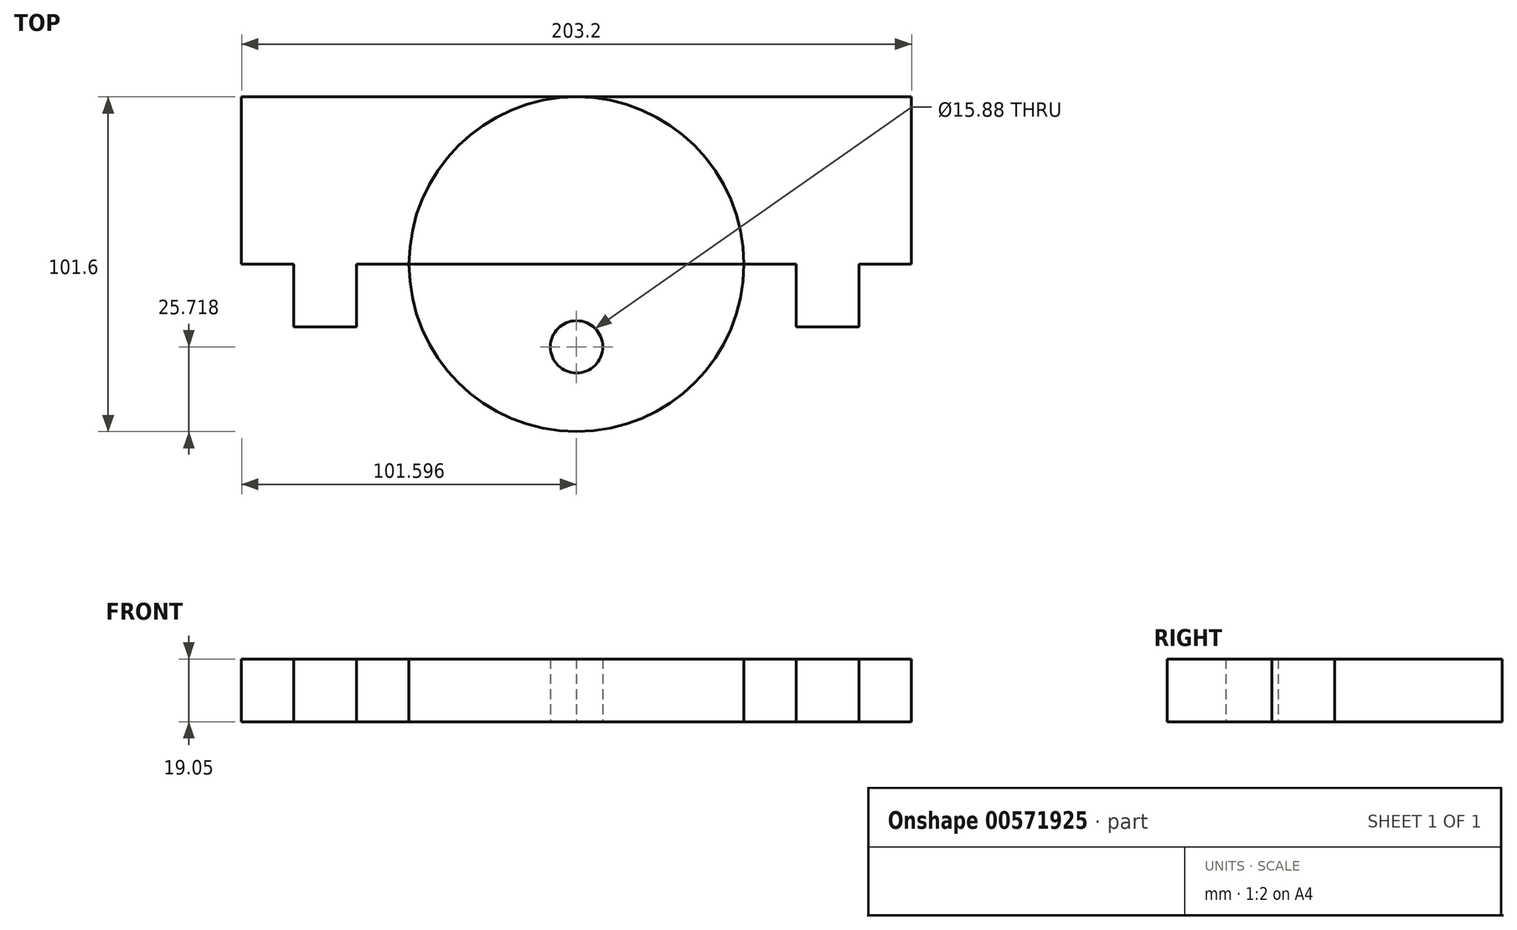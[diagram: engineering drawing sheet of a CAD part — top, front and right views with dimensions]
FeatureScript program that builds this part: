
annotation { "Feature Type Name" : "Feature", "Feature Type Description" : "" }
export const myFeature = defineFeature(function(context is Context, id is Id, definition is map)
    precondition{}
    {
        {
            var Q0;
            Q0=qCreatedBy(makeId("Top.planeOp"),FACE);
            var sketch = newSketch(context, id + "F0", { "sketchPlane" : qUnion([Q0])});
            skLineSegment(sketch, "E0.bottom", {"start": v(-100.72, 0) * mm, "end": v(-303.92, 0) * mm});
            skLineSegment(sketch, "E0.top", {"start": v(-100.72, -50.8) * mm, "end": v(-303.92, -50.8) * mm});
            skLineSegment(sketch, "E0.left", {"start": v(-100.72, 0) * mm, "end": v(-100.72, -50.8) * mm});
            skLineSegment(sketch, "E0.right", {"start": v(-303.92, 0) * mm, "end": v(-303.92, -50.8) * mm});
            skCircle(sketch, "E1", {"center": v(-202.32, -50.8) * mm, "radius": 50.8 * mm});
            skCircle(sketch, "E2", {"center": v(-202.32, -75.88) * mm, "radius": 7.94 * mm});
            skSolve(sketch);
        }
        {
            var Q0;
            {var subQ0=sQuery(id+"F0.wireOp",EDGE,"E0.right");Q0=makeQuery(id+"F0.imprint","IMPRINT",FACE,{"disambiguationData":[TD([[makeQuery(id+"F0.imprint","IMPRINT",EDGE,{"derivedFrom":subQ0}),1.0]])]});}
            var Q1;
            {var subQ0=sQuery(id+"F0.wireOp",EDGE,"E1");var subQ1=sQuery(id+"F0.wireOp",EDGE,"E0.top");var subQ2=makeQuery(id+"F0.imprint","INTERSECT",VERTEX,{"disambiguationData":[OD(0.0)],"derivedFrom":[subQ1,subQ0]});Q1=makeQuery(id+"F0.imprint","IMPRINT",FACE,{"disambiguationData":[TD([[makeQuery(id+"F0.imprint","IMPRINT",EDGE,{"disambiguationData":[TD([[subQ2,-1.0]])],"derivedFrom":subQ1}),-1.0]])]});}
            var Q2;
            {var subQ0=sQuery(id+"F0.wireOp",EDGE,"E0.left");Q2=makeQuery(id+"F0.imprint","IMPRINT",FACE,{"disambiguationData":[TD([[makeQuery(id+"F0.imprint","IMPRINT",EDGE,{"derivedFrom":subQ0}),-1.0]])]});}
            var Q3;
            Q3=makeQuery(id+"F0.imprint","IMPRINT",FACE,{"disambiguationData":[TD([[makeQuery(id+"F0.imprint","IMPRINT",EDGE,{"derivedFrom":sQuery(id+"F0.wireOp",EDGE,"E2")}),-1.0]])]});
            extrude(context, id + "F1", {"entities" : qUnion([Q0, Q1, Q2, Q3]), "depth" : 19.05 * mm, "offsetDistance" : 25.4 * mm});
        }
        {
            var Q0;
            {var subQ0=sQuery(id+"F0.wireOp",EDGE,"E0.top");Q0=makeQuery(id+"F1.opExtrude","SWEPT_FACE",FACE,{"disambiguationData":[OSD([subQ0]),TDD([makeQuery(id+"F0.imprint","IMPRINT",EDGE,{"disambiguationData":[TD([[makeQuery(id+"F0.imprint","INTERSECT",VERTEX,{"derivedFrom":[subQ0,sQuery(id+"F0.wireOp",EDGE,"E0.right")]}),1.0]])],"derivedFrom":subQ0})])]});}
            var sketch = newSketch(context, id + "F2", { "sketchPlane" : qUnion([Q0])});
            skLineSegment(sketch, "E3.bottom", {"start": v(-288.05, 19.05) * mm, "end": v(-269, 19.05) * mm});
            skLineSegment(sketch, "E3.top", {"start": v(-288.05, 0) * mm, "end": v(-269, 0) * mm});
            skLineSegment(sketch, "E3.left", {"start": v(-288.05, 19.05) * mm, "end": v(-288.05, 0) * mm});
            skLineSegment(sketch, "E3.right", {"start": v(-269, 19.05) * mm, "end": v(-269, 0) * mm});
            skLineSegment(sketch, "E4.bottom", {"start": v(-135.65, 19.05) * mm, "end": v(-116.6, 19.05) * mm});
            skLineSegment(sketch, "E4.top", {"start": v(-135.65, 0) * mm, "end": v(-116.6, 0) * mm});
            skLineSegment(sketch, "E4.left", {"start": v(-135.65, 19.05) * mm, "end": v(-135.65, 0) * mm});
            skLineSegment(sketch, "E4.right", {"start": v(-116.6, 19.05) * mm, "end": v(-116.6, 0) * mm});
            skLineSegment(sketch, "E5.0.0", {"start": v(-303.92, 19.05) * mm, "end": v(-253.12, 19.05) * mm});
            skLineSegment(sketch, "E5.0.1", {"start": v(-253.12, 19.05) * mm, "end": v(-151.52, 19.05) * mm});
            skLineSegment(sketch, "E5.0.2", {"start": v(-151.52, 19.05) * mm, "end": v(-100.72, 19.05) * mm});
            skLineSegment(sketch, "E5.0.4", {"start": v(-100.72, 19.05) * mm, "end": v(-303.92, 19.05) * mm});
            skSolve(sketch);
        }
        {
            var Q0;
            Q0=makeQuery(id+"F2.imprint","IMPRINT",FACE,{"disambiguationData":[TD([[makeQuery(id+"F2.imprint","IMPRINT",EDGE,{"derivedFrom":sQuery(id+"F2.wireOp",EDGE,"E3.bottom")}),1.0]])]});
            var Q1;
            Q1=makeQuery(id+"F2.imprint","IMPRINT",FACE,{"disambiguationData":[TD([[makeQuery(id+"F2.imprint","IMPRINT",EDGE,{"derivedFrom":sQuery(id+"F2.wireOp",EDGE,"E4.bottom")}),-1.0]])]});
            extrude(context, id + "F3", {"entities" : qUnion([Q0, Q1]), "operationType" : NewBodyOperationType.ADD, "depth" : 19.05 * mm, "offsetDistance" : 25.4 * mm});
        }
    });
